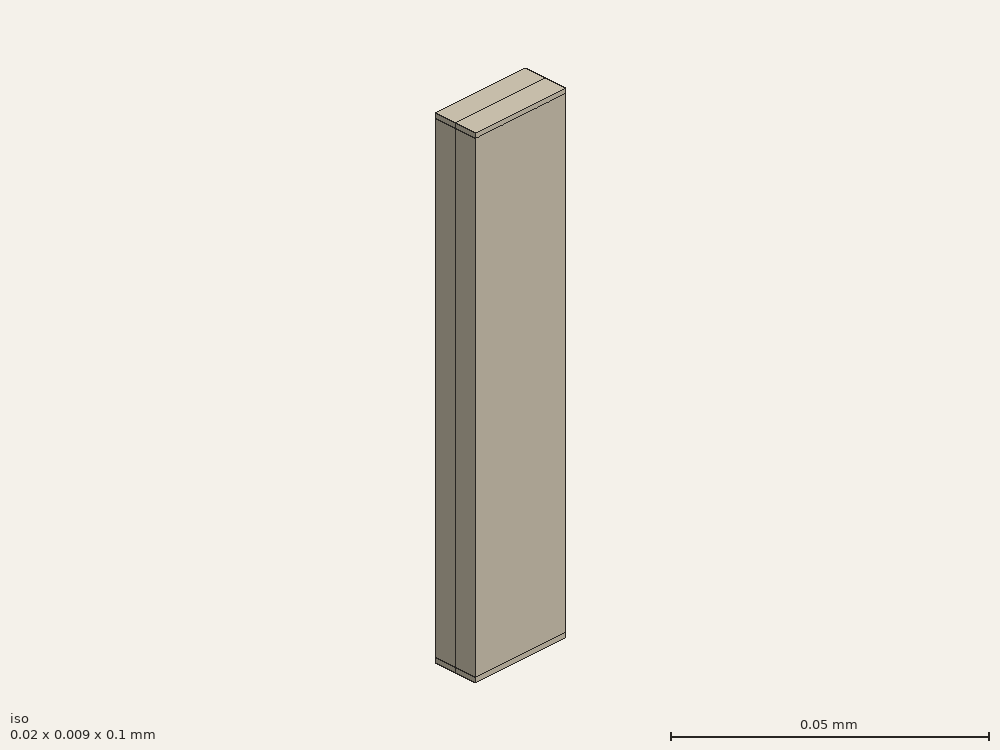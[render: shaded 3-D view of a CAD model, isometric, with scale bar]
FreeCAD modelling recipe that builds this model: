
FCSTD DOCUMENT  (FreeCAD 0.21R33694 (Git))
Label: partially_filled_waveguide
License: All rights reserved
LicenseURL: http://en.wikipedia.org/wiki/All_rights_reserved
objects: Part::Part2DObjectPython×10, App::FeaturePython×8, Part::Extrusion×2, Part::FeaturePython×1
note: 13 computed .brp shape members not serialized (recipe doc carries the construction recipe); baked Part::Feature solids carry a one-line shape summary decoded from their .brp

FEATURE [Part::Part2DObjectPython] Rectangle  label="air"  # Draft 2D object (typed FeaturePython)
  Area = 9e-05
  ChamferSize = 0
  Columns = 1
  FilletRadius = 0
  Height = 0.0045
  Length = 0.02
  MakeFace = true
  Placement = pos=(0,0.0045,0) rot=(0,0,1;0rad)
  Rows = 1
FEATURE [Part::Part2DObjectPython] Rectangle001  label="teflon"  # Draft 2D object (typed FeaturePython)
  Area = 9e-05
  ChamferSize = 0
  Columns = 1
  FilletRadius = 0
  Height = 0.0045
  Length = 0.02
  MakeFace = true
  Rows = 1
FEATURE [Part::Extrusion] Extrude
  Base = -> Rectangle
  Dir = (0,0,1)
  DirMode = 2
  FaceMakerClass = Part::FaceMakerBullseye
  LengthFwd = 0.1
  LengthRev = 0
  Solid = false
  Symmetric = false
FEATURE [Part::Extrusion] Extrude001
  Base = -> Rectangle001
  Dir = (0,0,1)
  DirMode = 2
  FaceMakerClass = Part::FaceMakerBullseye
  LengthFwd = 0.1
  LengthRev = 0
  Solid = false
  Symmetric = false
FEATURE [Part::Part2DObjectPython] Rectangle003  label="_P2"  # Draft 2D object (typed FeaturePython)
  Area = 0.00018
  ChamferSize = 0
  Columns = 1
  FilletRadius = 0
  Height = 0.009
  Length = 0.02
  MakeFace = true
  Placement = pos=(0,0,0.1) rot=(0,0,1;0rad)
  Rows = 1
FEATURE [Part::Part2DObjectPython] Line001  label="_Pv2"  # Draft 2D object (typed FeaturePython)
  Area = 0
  ChamferSize = 0
  Closed = false
  End = (0.01,0.009,0.1)
  FilletRadius = 0
  Length = 0.009
  MakeFace = true
  Placement = pos=(0.01,0,0.1) rot=(0,0,1;0rad)
  Points = (2) [(0,0,0),(0,0.009,0)]
  Start = (0.01,0,0.1)
  Subdivisions = 0
FEATURE [App::FeaturePython] Text  label="_S1(PV){1}"  # WARN: FeaturePython — macro-defined, semantics opaque (R4)
  Placement = pos=(0.0691109,-0.0323124,0) rot=(0,0,1;0rad)
  Text = .
FEATURE [App::FeaturePython] Text001  label="_S2(PV){2}"  # WARN: FeaturePython — macro-defined, semantics opaque (R4)
  Placement = pos=(0.0691109,-0.0323124,0) rot=(0,0,1;0rad)
  Text = .
FEATURE [App::FeaturePython] Text002  label="_L1(1,voltage){v1}"  # WARN: FeaturePython — macro-defined, semantics opaque (R4)
  Placement = pos=(0.0691109,-0.0323124,0) rot=(0,0,1;0rad)
  Text = .
FEATURE [App::FeaturePython] Text003  label="_L2(2,voltage){v2}"  # WARN: FeaturePython — macro-defined, semantics opaque (R4)
  Placement = pos=(0.0691109,-0.0323124,0) rot=(0,0,1;0rad)
  Text = .
FEATURE [Part::Part2DObjectPython] Rectangle004  label="_P1"  # Draft 2D object (typed FeaturePython)
  Area = 0.00018
  ChamferSize = 0
  Columns = 1
  FilletRadius = 0
  Height = 0.009
  Length = 0.02
  MakeFace = true
  Rows = 1
FEATURE [Part::Part2DObjectPython] Line  label="_Pv1"  # Draft 2D object (typed FeaturePython)
  Area = 0
  ChamferSize = 0
  Closed = false
  End = (0.01,0.009,0)
  FilletRadius = 0
  Length = 0.009
  MakeFace = true
  Placement = pos=(0.01,0,0) rot=(0,0,1;0rad)
  Points = (2) [(0,0,0),(0,0.009,0)]
  Start = (0.01,0,0)
  Subdivisions = 0
FEATURE [App::FeaturePython] Text004  label="_Bt(SI,copper){t}"  # WARN: FeaturePython — macro-defined, semantics opaque (R4)
  Placement = pos=(0.0691109,-0.0323124,0) rot=(0,0,1;0rad)
  Text = .
FEATURE [App::FeaturePython] Text005  label="_Bb(SI,copper){b}"  # WARN: FeaturePython — macro-defined, semantics opaque (R4)
  Placement = pos=(0.0691109,-0.0323124,0) rot=(0,0,1;0rad)
  Text = .
FEATURE [App::FeaturePython] Text006  label="_Br(SI,copper){r}"  # WARN: FeaturePython — macro-defined, semantics opaque (R4)
  Placement = pos=(0.0691109,-0.0323124,0) rot=(0,0,1;0rad)
  Text = .
FEATURE [App::FeaturePython] Text007  label="_Bl(SI,copper){l}"  # WARN: FeaturePython — macro-defined, semantics opaque (R4)
  Placement = pos=(0.0691109,-0.0323124,0) rot=(0,0,1;0rad)
  Text = .
FEATURE [Part::Part2DObjectPython] Rectangle009  label="_Pt"  # Draft 2D object (typed FeaturePython)
  Area = 0.00196
  ChamferSize = 0
  Columns = 1
  FilletRadius = 0
  Height = 0.098
  Length = 0.02
  MakeFace = true
  Placement = pos=(0,0,0.001) rot=(1,0,0;1.5708rad)
  Rows = 1
FEATURE [Part::Part2DObjectPython] Rectangle010  label="_Pb"  # Draft 2D object (typed FeaturePython)
  Area = 0.00196
  ChamferSize = 0
  Columns = 1
  FilletRadius = 0
  Height = 0.098
  Length = 0.02
  MakeFace = true
  Placement = pos=(0,0.009,0.001) rot=(1,0,0;1.5708rad)
  Rows = 1
FEATURE [Part::Part2DObjectPython] Rectangle011  label="_Pr"  # Draft 2D object (typed FeaturePython)
  Area = 0.000882
  ChamferSize = 0
  Columns = 1
  FilletRadius = 0
  Height = 0.098
  Length = 0.009
  MakeFace = true
  Placement = pos=(0.02,0,0.001) rot=(0.57735,0.57735,0.57735;2.0944rad)
  Rows = 1
FEATURE [Part::Part2DObjectPython] Rectangle012  label="_Pl"  # Draft 2D object (typed FeaturePython)
  Area = 0.000882
  ChamferSize = 0
  Columns = 1
  FilletRadius = 0
  Height = 0.098
  Length = 0.009
  MakeFace = true
  Placement = pos=(0,0.009,0.001) rot=(0.57735,-0.57735,-0.57735;2.0944rad)
  Rows = 1
FEATURE [Part::FeaturePython] BooleanFragments  # WARN: FeaturePython — macro-defined, semantics opaque (R4)
  Mode = 0
  Objects = -> [Extrude,Extrude001,Rectangle009,Rectangle010,Rectangle011,Rectangle012]
  Tolerance = 0
